# Revit family: 28L 2 to 6 units single sided Outdoor Manifold System123
name_source: partatom
category: Plumbing Fixtures
revit_build: Autodesk Revit 2017 (Build: 20160225_1515(x64)
units: mm (PartAtom-declared; Revit-internal decimal feet)

## family parameters
Always vertical = Yes
Cut with Voids When Loaded = No
Part Type = Normal
Room Calculation Point = No
Round Connector Dimension = Use Diameter
Shared = No
Work Plane-Based = No

## types (10) — shared parameters
Cold Water Inlet Pipe connector description = Male threaded connector R1-1/2"
Cold Water Inlet Pipe diameter = 38.1mm(DN 40)
Gas Inlet Pipe connector description = Male threaded connector R1-1/2"
Gas Inlet Pipe diameter = 38.1mm(DN 40)
Hot Water Outlet Pipe connector description = Male threaded connector R1-1/2"
Hot Water Outlet Pipe diameter = 38.1mm(DN 40)

## per-type parameters (varying)
- 28L 2 units single sided outdoor floor mounted: 2 Unit L=Yes; 2 Unit R=No; 3 Unit L=No; 3 Unit R=No; Array Offset=360.00 mm; Base Offset L=794.00 mm; Base Offset R=1040.00 mm; Base Support L=Yes; Base Support R=No; Connector Left=2324.00 mm; Connector Right=1550.00 mm; D1=1757.00 mm; D2=217.00 mm; D3=1757.00 mm; No of Connectors 1=2; No of Connectors 2=2; No. of power supply point required=2; Nominal depth=900mm; Nominal height=1540mm; Nominal width=794mm; Number of Gas Water Heaters=2; Product SKU Dux brand=D22800EN/LFx; Product SKU Thermann brand=T22800EN/LFx; Product description=Gas Water heater Manifold 2 unit outdoor floor mounted; Total Max. power requirement=386W; Total nominal gas consumption (MJ/h)=440; Unit Offset=41.30 mm; Weight (Kg)=90
- 28L 3 units single sided outdoor floor mounted: 2 Unit L=No; 2 Unit R=No; 3 Unit L=Yes; 3 Unit R=No; Array Offset=360.00 mm; Base Offset L=1170.00 mm; Base Offset R=1040.00 mm; Base Support L=Yes; Base Support R=No; Connector Left=2700.00 mm; Connector Right=1550.00 mm; D1=2125.00 mm; D2=225.00 mm; D3=1765.00 mm; No of Connectors 1=3; No of Connectors 2=3; No. of power supply point required=3; Nominal depth=900mm; Nominal height=1540mm; Nominal width=1170mm; Number of Gas Water Heaters=3; Product SKU Dux brand=D32800EN/LFx; Product SKU Thermann brand=T32800EN/LFx; Product description=Gas Water heater Manifold 3 unit outdoor floor mounted; Total Max. power requirement=579W; Total nominal gas consumption (MJ/h)=660; Unit Offset=41.30 mm; Weight (Kg)=120
- 28L 4 units single sided outdoor floor mounted: 2 Unit L=Yes; 2 Unit R=Yes; 3 Unit L=No; 3 Unit R=No; Array Offset=360.00 mm; Base Offset L=794.00 mm; Base Offset R=794.00 mm; Base Support L=Yes; Base Support R=Yes; Connector Left=2324.00 mm; Connector Right=756.00 mm; D1=963.00 mm; D2=217.00 mm; D3=963.00 mm; No of Connectors 1=2; No of Connectors 2=2; No. of power supply point required=4; Nominal depth=900mm; Nominal height=1540mm; Nominal width=1588mm; Number of Gas Water Heaters=4; Product SKU Dux brand=D42800EN/LFx; Product SKU Thermann brand=T42800EN/LFx; Product description=Gas Water heater Manifold 4 unit outdoor floor mounted; Total Max. power requirement=772W; Total nominal gas consumption (MJ/h)=880; Unit Offset=41.30 mm; Weight (Kg)=180
- 28L 5 units single sided outdoor floor mounted: 2 Unit L=No; 2 Unit R=Yes; 3 Unit L=Yes; 3 Unit R=No; Array Offset=360.00 mm; Base Offset L=1170.00 mm; Base Offset R=794.00 mm; Base Support L=Yes; Base Support R=Yes; Connector Left=2700.00 mm; Connector Right=756.00 mm; D1=2125.00 mm; D2=225.00 mm; D3=963.00 mm; No of Connectors 1=2; No of Connectors 2=3; No. of power supply point required=5; Nominal depth=900mm; Nominal height=1540mm; Nominal width=1964mm; Number of Gas Water Heaters=5; Product SKU Dux brand=D52800EN/LFx; Product SKU Thermann brand=T52800EN/LFx; Product description=Gas Water heater Manifold 5 unit outdoor floor mounted; Total Max. power requirement=965W; Total nominal gas consumption (MJ/h)=1100; Unit Offset=41.30 mm; Weight (Kg)=210
- 28L 6 units single sided outdoor floor mounted: 2 Unit L=No; 2 Unit R=No; 3 Unit L=Yes; 3 Unit R=Yes; Array Offset=1170.00 mm; Base Offset L=1170.00 mm; Base Offset R=1170.00 mm; Base Support L=Yes; Base Support R=Yes; Connector Left=2700.00 mm; Connector Right=380.00 mm; D1=1315.00 mm; D2=225.00 mm; D3=595.00 mm; No of Connectors 1=3; No of Connectors 2=3; No. of power supply point required=6; Nominal depth=900mm; Nominal height=1540mm; Nominal width=2340mm; Number of Gas Water Heaters=6; Product SKU Dux brand=D62800EN/LFx; Product SKU Thermann brand=T62800EN/LFx; Product description=Gas Water heater Manifold 6 unit  outdoor floor mounted; Total Max. power requirement=1158W; Total nominal gas consumption (MJ/h)=1320; Unit Offset=41.30 mm; Weight (Kg)=240
- 28L 2 units single sided outdoor wall mounted: 2 Unit L=Yes; 2 Unit R=No; 3 Unit L=No; 3 Unit R=No; Array Offset=360.00 mm; Base Offset L=1040.00 mm; Base Offset R=1040.00 mm; Base Support L=No; Base Support R=No; Connector Left=2324.00 mm; Connector Right=1550.00 mm; D1=1757.00 mm; D2=217.00 mm; D3=1757.00 mm; No of Connectors 1=2; No of Connectors 2=2; No. of power supply point required=2; Nominal depth=303mm; Nominal height=1500mm; Nominal width=794mm; Number of Gas Water Heaters=2; Product SKU Dux brand=D22800EN/LWx; Product SKU Thermann brand=T22800EN/LWx; Product description=Gas Water heater Manifold 2 unit outdoor wall mounted; Total Max. power requirement=386W; Total nominal gas consumption (MJ/h)=440; Unit Offset=0.00 mm; Weight (Kg)=90
- 28L 3 units single sided outdoor wall mounted: 2 Unit L=No; 2 Unit R=No; 3 Unit L=Yes; 3 Unit R=No; Array Offset=360.00 mm; Base Offset L=1540.00 mm; Base Offset R=1040.00 mm; Base Support L=No; Base Support R=No; Connector Left=2700.00 mm; Connector Right=1550.00 mm; D1=2125.00 mm; D2=225.00 mm; D3=1765.00 mm; No of Connectors 1=3; No of Connectors 2=3; No. of power supply point required=3; Nominal depth=303mm; Nominal height=1500mm; Nominal width=1170mm; Number of Gas Water Heaters=3; Product SKU Dux brand=D32800EN/LWx; Product SKU Thermann brand=T32800EN/LWx; Product description=Gas Water heater Manifold 3 unit outdoor wall mounted; Total Max. power requirement=579W; Total nominal gas consumption (MJ/h)=660; Unit Offset=0.00 mm; Weight (Kg)=120
- 28L 4 units single sided outdoor wall mounted: 2 Unit L=Yes; 2 Unit R=Yes; 3 Unit L=No; 3 Unit R=No; Array Offset=360.00 mm; Base Offset L=1040.00 mm; Base Offset R=1040.00 mm; Base Support L=No; Base Support R=No; Connector Left=2324.00 mm; Connector Right=756.00 mm; D1=963.00 mm; D2=217.00 mm; D3=963.00 mm; No of Connectors 1=2; No of Connectors 2=2; No. of power supply point required=4; Nominal depth=303mm; Nominal height=1500mm; Nominal width=1588mm; Number of Gas Water Heaters=4; Product SKU Dux brand=D42800EN/LWx; Product SKU Thermann brand=T42800EN/LWx; Product description=Gas Water heater Manifold 4 unit outdoor wall mounted; Total Max. power requirement=772W; Total nominal gas consumption (MJ/h)=880; Unit Offset=0.00 mm; Weight (Kg)=180
- 28L 5 units single sided outdoor wall mounted: 2 Unit L=No; 2 Unit R=Yes; 3 Unit L=Yes; 3 Unit R=No; Array Offset=360.00 mm; Base Offset L=1540.00 mm; Base Offset R=1040.00 mm; Base Support L=No; Base Support R=No; Connector Left=2700.00 mm; Connector Right=756.00 mm; D1=2125.00 mm; D2=225.00 mm; D3=963.00 mm; No of Connectors 1=2; No of Connectors 2=3; No. of power supply point required=5; Nominal depth=303mm; Nominal height=1500mm; Nominal width=1964mm; Number of Gas Water Heaters=5; Product SKU Dux brand=D52800EN/LWx; Product SKU Thermann brand=T52800EN/LWx; Product description=Gas Water heater Manifold 5 unit  outdoor wall mounted; Total Max. power requirement=965W; Total nominal gas consumption (MJ/h)=1100; Unit Offset=0.00 mm; Weight (Kg)=210
- 28L 6 units single sided outdoor wall mounted: 2 Unit L=No; 2 Unit R=No; 3 Unit L=Yes; 3 Unit R=Yes; Array Offset=1170.00 mm; Base Offset L=1040.00 mm; Base Offset R=1040.00 mm; Base Support L=No; Base Support R=No; Connector Left=2700.00 mm; Connector Right=380.00 mm; D1=1315.00 mm; D2=225.00 mm; D3=595.00 mm; No of Connectors 1=3; No of Connectors 2=3; No. of power supply point required=6; Nominal depth=303mm; Nominal height=1500mm; Nominal width=2340mm; Number of Gas Water Heaters=6; Product SKU Dux brand=D62800EN/LWx; Product SKU Thermann brand=T62800EN/LWx; Product description=Gas Water heater Manifold 6 unit outdoor wall mounted; Total Max. power requirement=1158W; Total nominal gas consumption (MJ/h)=1320; Unit Offset=0.00 mm; Weight (Kg)=240

## geometry (parser evidence)
native form markers: Sweep x10
no freeform markers — native parametric forms only
